# Revit family: Thorn EQUALINE
name_source: partatom
category: Lighting Fixtures
revit_build: Autodesk Revit 2016 (Build: 20150220_1215(x64)
units: mm (PartAtom-declared; Revit-internal decimal feet)

## family parameters
Cut with Voids When Loaded = No
Host = Face
Light Source = Yes
OmniClass Number = 23.80.70.11
OmniClass Title = Luminaries for Internal Lighting
Part Type = Normal
Room Calculation Point = No
Round Connector Dimension = Use Diameter
Shared = No

## types (21) — shared parameters
Assembly Code = D5020200
Color Filter = 16777215
Color Light Emitting Surface = Thorn_PMMA_White
Description = LED light line
Dimming Lamp Color Temperature Shift = <None>
Emit Shape Visible in Rendering = No
Emit from Rectangle Length = 72 mm  [stored 0.23622 ft]
Height = 88 mm  [stored 0.288714 ft]
Lamp = LED
Manufacturer = Thorn Lighting
Tilt Angle = -90.00°
URL = http://www.thornlighting.com
Voltage = 230 V
Width = 72 mm  [stored 0.23622 ft]
zero-valued in all types: Default Elevation

## per-type parameters (varying)
| type | Apparent Load | Body | Emit from Rectangle Width | F Frame | FS Frame | Length | Model | Photometric Web File |
| EQL L1000 | 22 VA | Thorn_Metal_Silver | 1000 mm  [stored 3.28084 ft] | No | No | 1000 mm  [stored 3.28084 ft] | 96631993 | D41200AA_EQL_C_L1000_840_PM_SR.IES |
| EQL L1250 | 25 VA | Thorn_Metal_Silver | 1250 mm  [stored 4.10105 ft] | No | No | 1250 mm  [stored 4.10105 ft] | 96631994 | D41200AA_EQL_C_L1250_840_PM_SR.IES |
| EQL L3000 | 57 VA | Thorn_Metal_Silver | 3000 mm  [stored 9.84252 ft] | No | No | 3000 mm  [stored 9.84252 ft] | 96631998 | D41200AA_EQL_C_L3000_840_PM_SR.IES |
| EQL L2000 | 40 VA | Thorn_Metal_Silver | 2000 mm  [stored 6.56168 ft] | No | No | 2000 mm  [stored 6.56168 ft] | 96631997 | D41200AA_EQL_C_L2000_840_PM_SR.IES |
| EQL L1750 | 35 VA | Thorn_Metal_Silver | 1750 mm  [stored 5.74147 ft] | No | No | 1750 mm  [stored 5.74147 ft] | 96631996 | D41200AA_EQL_C_L1750_840_PM_SR.IES |
| EQL L1500 | 30 VA | Thorn_Metal_Silver | 1500 mm  [stored 4.92126 ft] | No | No | 1500 mm  [stored 4.92126 ft] | 96631995 | D41200AA_EQL_C_L1500_840_PM_SR.IES |
| EQL L3000 FS | 57 VA | Thorn_Metal_White | 3000 mm  [stored 9.84252 ft] | No | Yes | 3000 mm  [stored 9.84252 ft] | 96632040 | D41200AA_EQL_C_L3000_840_PM_SR.IES |
| EQL L3000 F | 57 VA | Thorn_Metal_White | 3000 mm  [stored 9.84252 ft] | Yes | No | 3000 mm  [stored 9.84252 ft] | 96632014 | D41197AA_EQL_C_L3000_840_PM_WH.IES |
| EQL L2000 FS | 40 VA | Thorn_Metal_Silver | 2000 mm  [stored 6.56168 ft] | No | Yes | 2000 mm  [stored 6.56168 ft] | 96632039 | D41200AA_EQL_C_L2000_840_PM_SR.IES |
| EQL L2000 F | 40 VA | Thorn_Metal_White | 2000 mm  [stored 6.56168 ft] | Yes | No | 2000 mm  [stored 6.56168 ft] | 96632013 | D41197AA_EQL_C_L2000_840_PM_WH.IES |
| EQL L1800 F | 36 VA | Thorn_Metal_White | 1800 mm  [stored 5.90551 ft] | Yes | No | 1800 mm  [stored 5.90551 ft] | 96632007 | D41197AA_EQL_C_L1800_840_PM_WH.IES |
| EQL L1750 FS | 35 VA | Thorn_Metal_White | 1750 mm  [stored 5.74147 ft] | No | Yes | 1750 mm  [stored 5.74147 ft] | 96632038 | D41200AA_EQL_C_L1750_840_PM_SR.IES |
| EQL L1750 F | 35 VA | Thorn_Metal_White | 1750 mm  [stored 5.74147 ft] | Yes | No | 1750 mm  [stored 5.74147 ft] | 96632012 | D41197AA_EQL_C_L1750_840_PM_WH.IES |
| EQL L1500 FS | 30 VA | Thorn_Metal_Silver | 1500 mm  [stored 4.92126 ft] | No | Yes | 1500 mm  [stored 4.92126 ft] | 96632037 | D41200AA_EQL_C_L1500_840_PM_SR.IES |
| EQL L1500 F | 30 VA | Thorn_Metal_White | 1500 mm  [stored 4.92126 ft] | Yes | No | 1500 mm  [stored 4.92126 ft] | 96632011 | D41197AA_EQL_C_L1500_840_PM_WH.IES |
| EQL L1250 FS | 25 VA | Thorn_Metal_Silver | 1250 mm  [stored 4.10105 ft] | No | Yes | 1250 mm  [stored 4.10105 ft] | 96632036 | D41200AA_EQL_C_L1250_840_PM_SR.IES |
| EQL L1250 F | 25 VA | Thorn_Metal_White | 1250 mm  [stored 4.10105 ft] | Yes | No | 1250 mm  [stored 4.10105 ft] | 96632010 | D41197AA_EQL_C_L1250_840_PM_WH.IES |
| EQL L1200 F | 24 VA | Thorn_Metal_White | 1200 mm | Yes | No | 1200 mm | 96632006 | D41197AA_EQL_C_L1200_840_PM_WH.IES |
| EQL L1000 FS | 22 VA | Thorn_Metal_Silver | 1000 mm  [stored 3.28084 ft] | No | Yes | 1000 mm  [stored 3.28084 ft] | 96632035 | D41200AA_EQL_C_L1000_840_PM_SR.IES |
| EQL L1000 F | 22 VA | Thorn_Metal_White | 1000 mm  [stored 3.28084 ft] | Yes | No | 1000 mm  [stored 3.28084 ft] | 96632009 | D41197AA_EQL_C_L1000_840_PM_WH.IES |
| EQL L600 F | 14 VA | Thorn_Metal_White | 600 mm | Yes | No | 600 mm | 96632005 | D41197AA_EQL_C_L600_840_PM_WH.IES |

note: [stored X ft] marks values corroborated as IEEE doubles in the binary element streams (Revit-internal decimal feet)

## geometry (parser evidence)
native form markers: Sweep x8
no freeform markers — native parametric forms only
